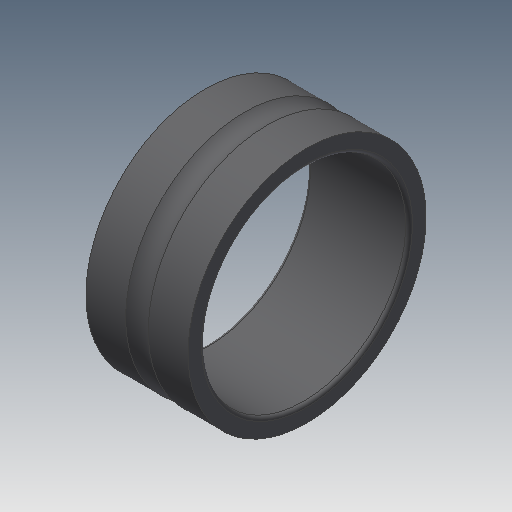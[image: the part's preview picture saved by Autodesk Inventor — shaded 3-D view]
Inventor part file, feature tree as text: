
AUTODESK INVENTOR PART (.ipt)
format: ipt  version: 2019.4 (Build 234330000, 330)  size: 204,800 bytes
history: native  units: mm
features: other x126, revolve x1, sketch x1
ambient origin geometry x8: Origin, YZ Plane, XZ Plane, XY Plane, X Axis, Y Axis, Z Axis, Center Point
bodies: Solid1 (feature_tree)
feature tree (128):
  revolve  "Revolution1"  [1 undecoded]
  other  "ip_st_1_1_XY"
  other  "ip_st_1_1_YZ"
  other  "ip_st_1_1_ZX"
  other  "ip_st_1_1_X"
  other  "ip_st_1_1_Y"
  other  "ip_st_1_1_Z"
  other  "ip_st_1_1_Center"
  other  "ip_st_1_10_XY"
  other  "ip_st_1_10_YZ"
  other  "ip_st_1_10_ZX"
  other  "ip_st_1_10_X"
  other  "ip_st_1_10_Y"
  other  "ip_st_1_10_Z"
  other  "ip_st_1_10_Center"
  other  "ip_st_1_11_XY"
  other  "ip_st_1_11_YZ"
  other  "ip_st_1_11_ZX"
  other  "ip_st_1_11_X"
  other  "ip_st_1_11_Y"
  other  "ip_st_1_11_Z"
  other  "ip_st_1_11_Center"
  other  "ip_st_1_12_XY"
  other  "ip_st_1_12_YZ"
  other  "ip_st_1_12_ZX"
  other  "ip_st_1_12_X"
  other  "ip_st_1_12_Y"
  other  "ip_st_1_12_Z"
  other  "ip_st_1_12_Center"
  other  "ip_st_1_13_XY"
  other  "ip_st_1_13_YZ"
  other  "ip_st_1_13_ZX"
  other  "ip_st_1_13_X"
  other  "ip_st_1_13_Y"
  other  "ip_st_1_13_Z"
  other  "ip_st_1_13_Center"
  other  "ip_st_1_14_XY"
  other  "ip_st_1_14_YZ"
  other  "ip_st_1_14_ZX"
  other  "ip_st_1_14_X"
  other  "ip_st_1_14_Y"
  other  "ip_st_1_14_Z"
  other  "ip_st_1_14_Center"
  other  "ip_st_1_15_XY"
  other  "ip_st_1_15_YZ"
  other  "ip_st_1_15_ZX"
  other  "ip_st_1_15_X"
  other  "ip_st_1_15_Y"
  other  "ip_st_1_15_Z"
  other  "ip_st_1_15_Center"
  other  "ip_st_1_16_XY"
  other  "ip_st_1_16_YZ"
  other  "ip_st_1_16_ZX"
  other  "ip_st_1_16_X"
  other  "ip_st_1_16_Y"
  other  "ip_st_1_16_Z"
  other  "ip_st_1_16_Center"
  other  "ip_st_1_2_XY"
  other  "ip_st_1_2_YZ"
  other  "ip_st_1_2_ZX"
  other  "ip_st_1_2_X"
  other  "ip_st_1_2_Y"
  other  "ip_st_1_2_Z"
  other  "ip_st_1_2_Center"
  other  "ip_st_1_3_XY"
  other  "ip_st_1_3_YZ"
  other  "ip_st_1_3_ZX"
  other  "ip_st_1_3_X"
  other  "ip_st_1_3_Y"
  other  "ip_st_1_3_Z"
  other  "ip_st_1_3_Center"
  other  "ip_st_1_4_XY"
  other  "ip_st_1_4_YZ"
  other  "ip_st_1_4_ZX"
  other  "ip_st_1_4_X"
  other  "ip_st_1_4_Y"
  other  "ip_st_1_4_Z"
  other  "ip_st_1_4_Center"
  other  "ip_st_1_5_XY"
  other  "ip_st_1_5_YZ"
  other  "ip_st_1_5_ZX"
  other  "ip_st_1_5_X"
  other  "ip_st_1_5_Y"
  other  "ip_st_1_5_Z"
  other  "ip_st_1_5_Center"
  other  "ip_st_1_6_XY"
  other  "ip_st_1_6_YZ"
  other  "ip_st_1_6_ZX"
  other  "ip_st_1_6_X"
  other  "ip_st_1_6_Y"
  other  "ip_st_1_6_Z"
  other  "ip_st_1_6_Center"
  other  "ip_st_1_7_XY"
  other  "ip_st_1_7_YZ"
  other  "ip_st_1_7_ZX"
  other  "ip_st_1_7_X"
  other  "ip_st_1_7_Y"
  other  "ip_st_1_7_Z"
  other  "ip_st_1_7_Center"
  other  "ip_st_1_8_XY"
  other  "ip_st_1_8_YZ"
  other  "ip_st_1_8_ZX"
  other  "ip_st_1_8_X"
  other  "ip_st_1_8_Y"
  other  "ip_st_1_8_Z"
  other  "ip_st_1_8_Center"
  other  "ip_st_1_9_XY"
  other  "ip_st_1_9_YZ"
  other  "ip_st_1_9_ZX"
  other  "ip_st_1_9_X"
  other  "ip_st_1_9_Y"
  other  "ip_st_1_9_Z"
  other  "ip_st_1_9_Center"
  other  "ip_st_1a_XY"
  other  "ip_st_1a_YZ"
  other  "ip_st_1a_ZX"
  other  "ip_st_1a_X"
  other  "ip_st_1a_Y"
  other  "ip_st_1a_Z"
  other  "ip_st_1a_Center"
  other  "ip_st_2a_XY"
  other  "ip_st_2a_YZ"
  other  "ip_st_2a_ZX"
  other  "ip_st_2a_X"
  other  "ip_st_2a_Y"
  other  "ip_st_2a_Z"
  other  "ip_st_2a_Center"
  sketch  "Sketch_1"  dims[d0=360.0deg d1=0.0mm]
note: 1 required parameter value undecoded (feature->parameter linkage not recoverable at this tier; creation-order binding heuristic only, values carry confidence <= 0.55)
